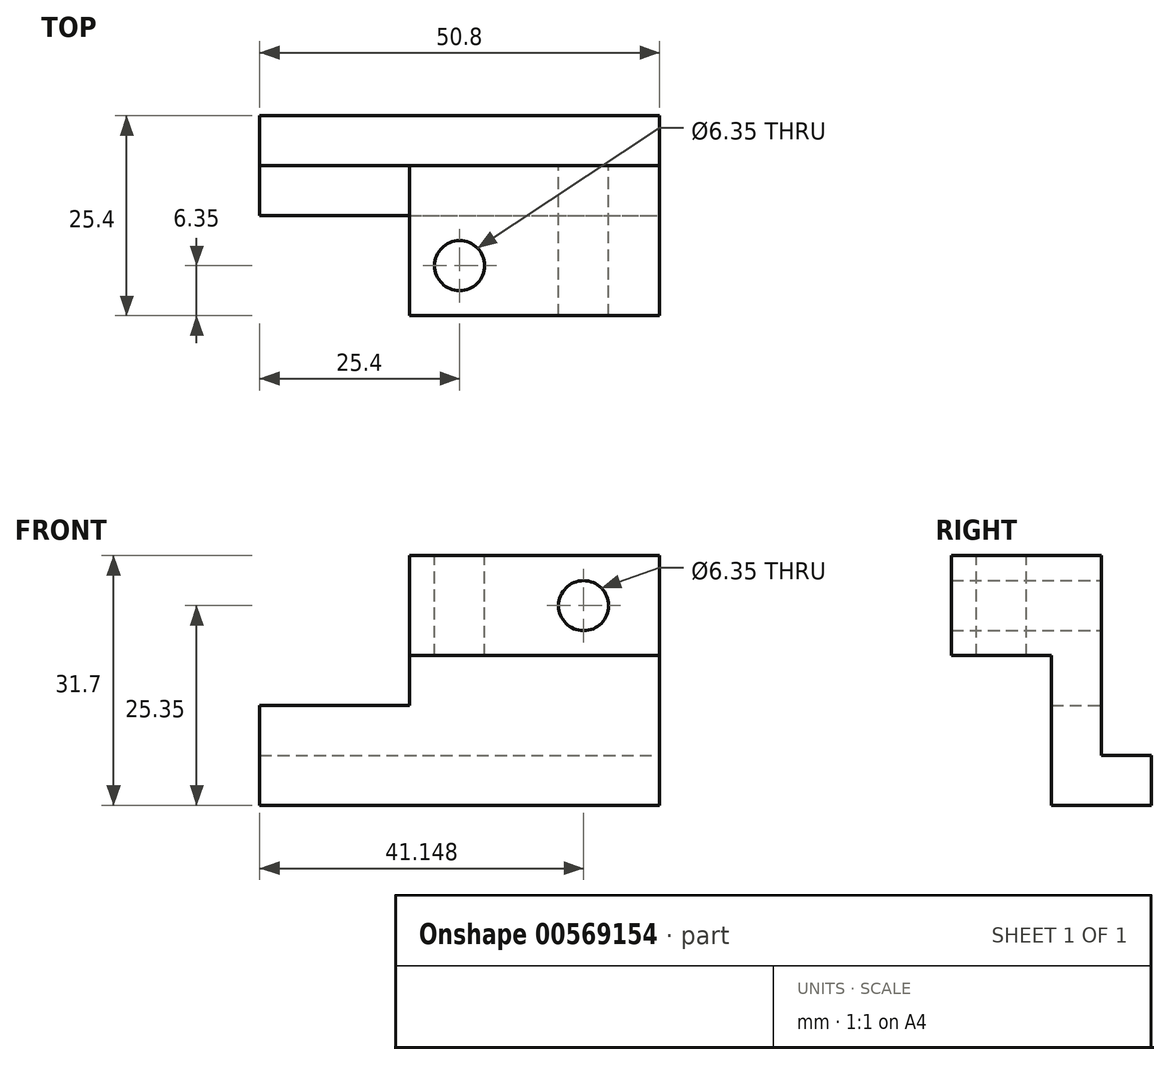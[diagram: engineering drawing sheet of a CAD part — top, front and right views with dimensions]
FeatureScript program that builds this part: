
annotation { "Feature Type Name" : "Feature", "Feature Type Description" : "" }
export const myFeature = defineFeature(function(context is Context, id is Id, definition is map)
    precondition{}
    {
        {
            var Q0;
            Q0=qCreatedBy(makeId("Right.planeOp"),FACE);
            var sketch = newSketch(context, id + "F0", { "sketchPlane" : qUnion([Q0])});
            skLineSegment(sketch, "E0", {"start": v(0, 0) * mm, "end": v(0, -12.7) * mm});
            skLineSegment(sketch, "E1", {"start": v(0, -12.7) * mm, "end": v(19.05, -12.7) * mm});
            skLineSegment(sketch, "E2", {"start": v(19.05, -12.7) * mm, "end": v(19.05, 0) * mm});
            skLineSegment(sketch, "E3", {"start": v(19.05, 0) * mm, "end": v(0, 0) * mm});
            skSolve(sketch);
        }
        {
            var Q0;
            Q0 = qSketchRegion(id + "F0", true);
            extrude(context, id + "F1", {"entities" : qUnion([Q0]), "depth" : 31.75 * mm, "offsetDistance" : 25.4 * mm});
        }
        {
            var Q0;
            Q0=makeQuery(id+"F1.opExtrude","CAP_FACE",FACE,{"disambiguationData":[OSD([sQuery(id+"F0.wireOp",EDGE,"E0"),sQuery(id+"F0.wireOp",EDGE,"E1"),sQuery(id+"F0.wireOp",EDGE,"E2"),sQuery(id+"F0.wireOp",EDGE,"E3")])],"isStart":false});
            var sketch = newSketch(context, id + "F2", { "sketchPlane" : qUnion([Q0])});
            skLineSegment(sketch, "E4", {"start": v(12.7, -19.05) * mm, "end": v(19.05, -19.05) * mm});
            skLineSegment(sketch, "E5", {"start": v(19.05, -12.7) * mm, "end": v(19.05, -19.05) * mm});
            skPoint(sketch, "E6.start.orphan", {"position": v(9.53, -12.7) * mm});
            skLineSegment(sketch, "E7", {"start": v(12.7, -19.05) * mm, "end": v(12.7, -12.7) * mm});
            skSolve(sketch);
        }
        {
            var Q0;
            Q0=makeQuery(id+"F2.imprint","IMPRINT",FACE,{"disambiguationData":[TD([[makeQuery(id+"F2.imprint","IMPRINT",EDGE,{"derivedFrom":sQuery(id+"F2.wireOp",EDGE,"E4")}),1.0]])]});
            extrude(context, id + "F3", {"entities" : qUnion([Q0]), "operationType" : NewBodyOperationType.ADD, "oppositeDirection" : true, "depth" : 31.75 * mm, "offsetDistance" : 25.4 * mm});
        }
        {
            var Q0;
            {var subQ0=sQuery(id+"F0.wireOp",EDGE,"E1");Q0=makeQuery(id+"F3.boolean.opBoolean","MERGE",FACE,{"derivedFrom":[makeQuery(id+"F1.opExtrude","CAP_FACE",FACE,{"disambiguationData":[OSD([sQuery(id+"F0.wireOp",EDGE,"E0"),subQ0,sQuery(id+"F0.wireOp",EDGE,"E2"),sQuery(id+"F0.wireOp",EDGE,"E3")])],"isStart":false}),makeQuery(id+"F3.opExtrude","CAP_FACE",FACE,{"disambiguationData":[OSD([subQ0,sQuery(id+"F2.wireOp",EDGE,"E4"),sQuery(id+"F2.wireOp",EDGE,"E5"),sQuery(id+"F2.wireOp",EDGE,"E7")])],"isStart":true})]});}
            var sketch = newSketch(context, id + "F4", { "sketchPlane" : qUnion([Q0])});
            skLineSegment(sketch, "E8", {"start": v(12.7, -19.05) * mm, "end": v(12.7, -31.7) * mm});
            skLineSegment(sketch, "E9", {"start": v(19.05, -19.05) * mm, "end": v(19.05, -25.4) * mm});
            skLineSegment(sketch, "E10", {"start": v(12.7, -31.7) * mm, "end": v(25.4, -31.7) * mm});
            skLineSegment(sketch, "E11", {"start": v(25.4, -31.7) * mm, "end": v(25.4, -25.35) * mm});
            skLineSegment(sketch, "E12", {"start": v(19.05, -25.4) * mm, "end": v(25.4, -25.35) * mm});
            skSolve(sketch);
        }
        {
            var Q0;
            Q0=makeQuery(id+"F4.imprint","IMPRINT",FACE,{"disambiguationData":[TD([[makeQuery(id+"F4.imprint","IMPRINT",EDGE,{"derivedFrom":sQuery(id+"F4.wireOp",EDGE,"E8")}),1.0]])]});
            extrude(context, id + "F5", {"entities" : qUnion([Q0]), "operationType" : NewBodyOperationType.ADD, "oppositeDirection" : true, "depth" : 50.8 * mm, "offsetDistance" : 25.4 * mm});
        }
        {
            var Q0;
            Q0=makeQuery(id+"F1.opExtrude","SWEPT_FACE",FACE,{"disambiguationData":[OSD([sQuery(id+"F0.wireOp",EDGE,"E3")])]});
            var sketch = newSketch(context, id + "F6", { "sketchPlane" : qUnion([Q0])});
            skCircle(sketch, "E13", {"center": v(6.35, 6.35) * mm, "radius": 3.18 * mm});
            skSolve(sketch);
        }
        {
            var Q0;
            Q0 = qSketchRegion(id + "F6", true);
            extrude(context, id + "F7", {"entities" : qUnion([Q0]), "operationType" : NewBodyOperationType.REMOVE, "endBound" : BoundingType.THROUGH_ALL, "oppositeDirection" : true, "depth" : 25.4 * mm, "offsetDistance" : 25.4 * mm});
        }
        {
            var Q0;
            Q0=makeQuery(id+"F5.boolean.opBoolean","MERGE",FACE,{"derivedFrom":[makeQuery(id+"F3.boolean.opBoolean","MERGE",FACE,{"derivedFrom":[makeQuery(id+"F1.opExtrude","SWEPT_FACE",FACE,{"disambiguationData":[OSD([sQuery(id+"F0.wireOp",EDGE,"E2")])]}),makeQuery(id+"F3.opExtrude","SWEPT_FACE",FACE,{"disambiguationData":[OSD([sQuery(id+"F2.wireOp",EDGE,"E5")])]})]}),makeQuery(id+"F5.opExtrude","SWEPT_FACE",FACE,{"disambiguationData":[OSD([sQuery(id+"F4.wireOp",EDGE,"E9")])]})]});
            var sketch = newSketch(context, id + "F8", { "sketchPlane" : qUnion([Q0])});
            skCircle(sketch, "E14", {"center": v(-22.1, -6.35) * mm, "radius": 3.18 * mm});
            skSolve(sketch);
        }
        {
            var Q0;
            Q0 = qSketchRegion(id + "F8", true);
            extrude(context, id + "F9", {"entities" : qUnion([Q0]), "operationType" : NewBodyOperationType.REMOVE, "oppositeDirection" : true, "depth" : 25.4 * mm, "offsetDistance" : 25.4 * mm});
        }
    });
